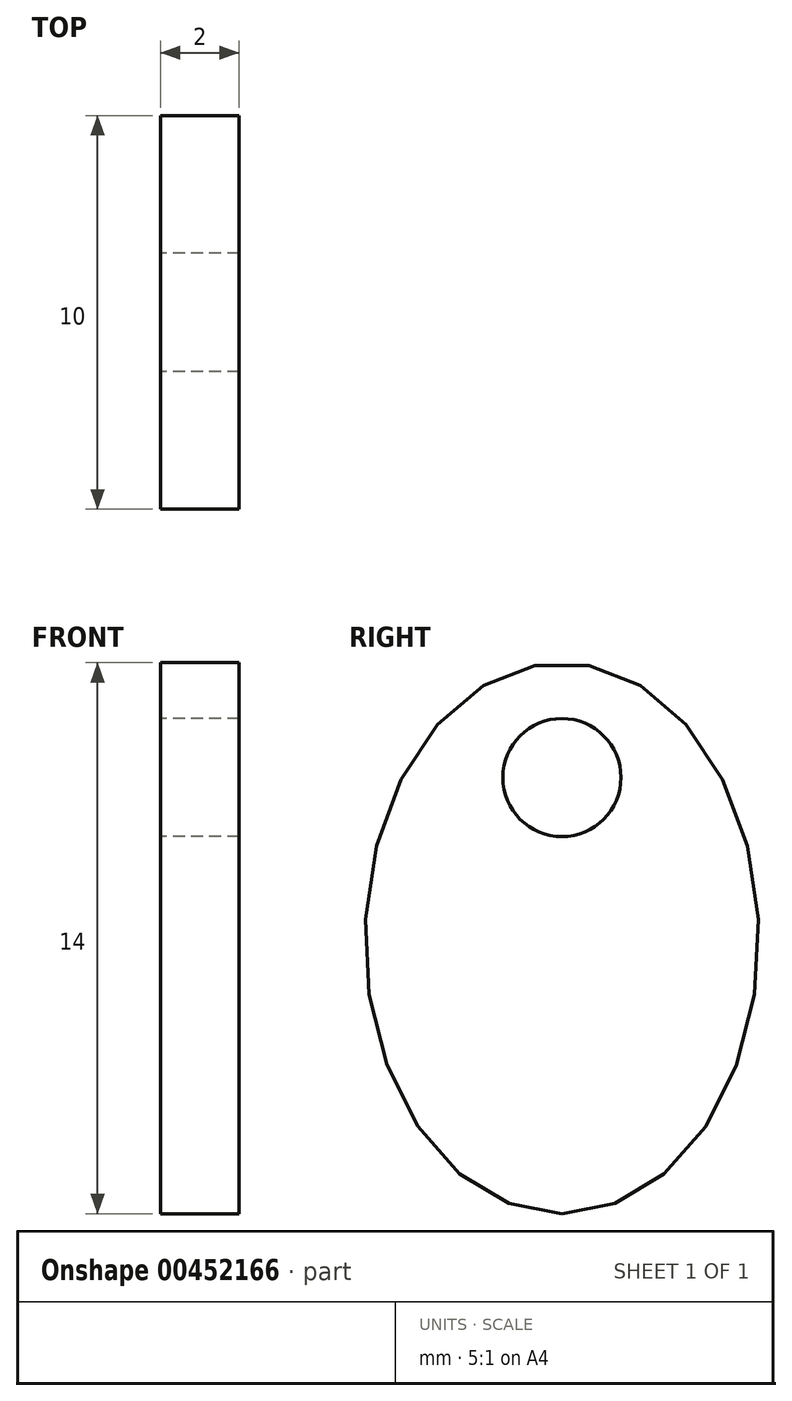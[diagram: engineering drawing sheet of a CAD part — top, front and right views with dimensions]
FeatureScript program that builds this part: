
annotation { "Feature Type Name" : "Feature", "Feature Type Description" : "" }
export const myFeature = defineFeature(function(context is Context, id is Id, definition is map)
    precondition{}
    {
        {
            var Q0;
            Q0=qCreatedBy(makeId("Right.planeOp"),FACE);
            var sketch = newSketch(context, id + "F0", { "sketchPlane" : qUnion([Q0])});
            skCircle(sketch, "E0", {"center": v(0, 0) * mm, "radius": 1.5 * mm});
            skEllipse(sketch, "E1", {"center": v(0, -4.08) * mm, "majorRadius": 7 * mm, "minorRadius": 5 * mm, "majorAxis": v(0, -1)});
            skSolve(sketch);
        }
        {
            var Q0;
            Q0 = qSketchRegion(id + "F0", true);
            extrude(context, id + "F1", {"entities" : qUnion([Q0]), "depth" : 2 * mm});
        }
    });
